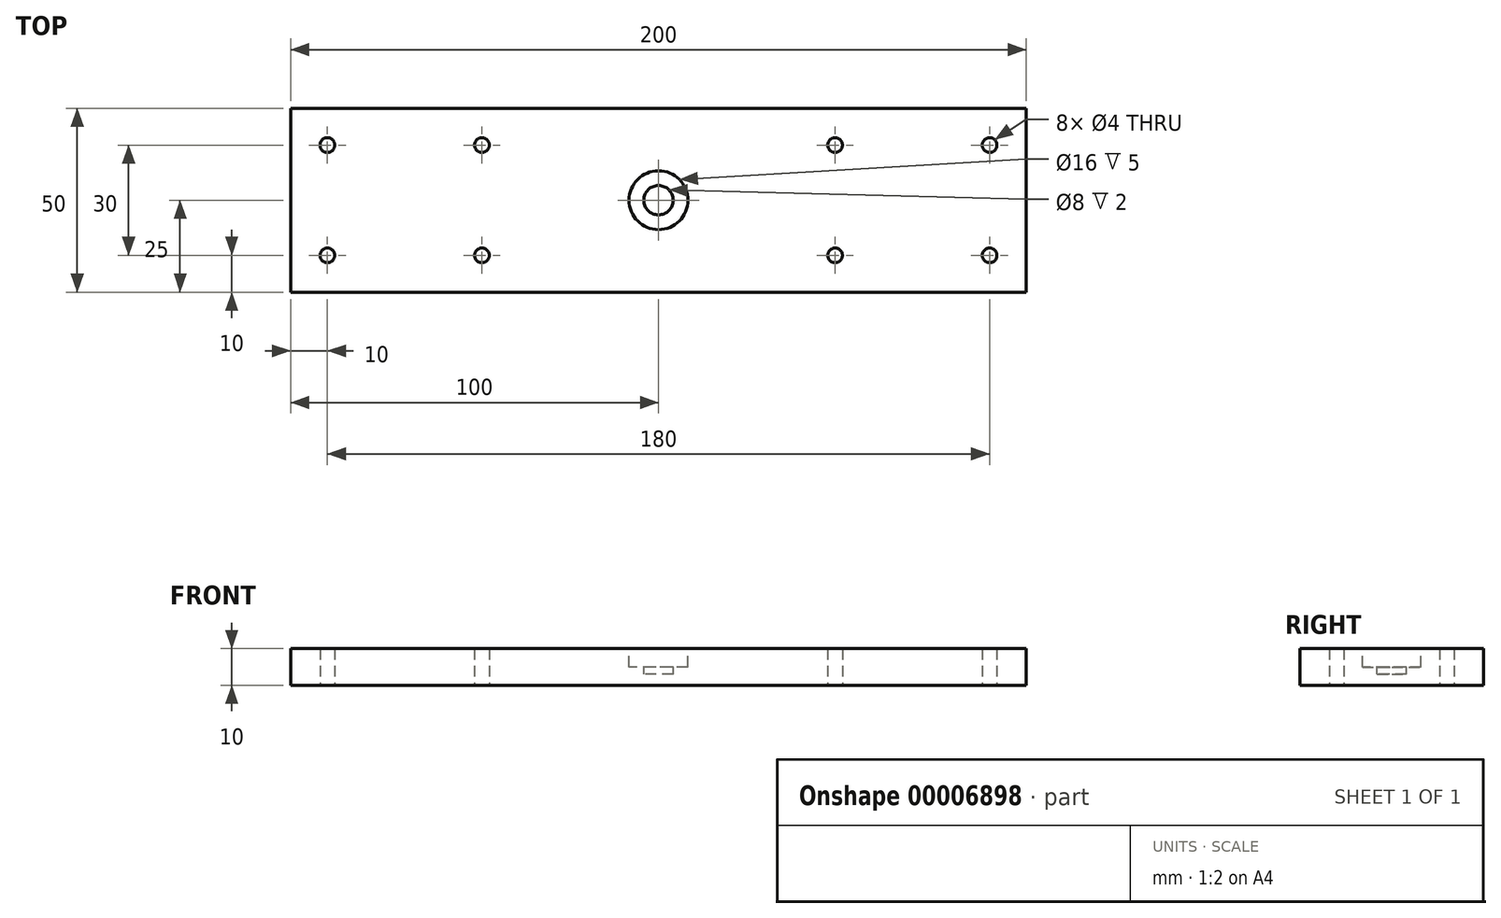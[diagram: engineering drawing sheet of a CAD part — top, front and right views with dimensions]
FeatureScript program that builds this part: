
annotation { "Feature Type Name" : "Feature", "Feature Type Description" : "" }
export const myFeature = defineFeature(function(context is Context, id is Id, definition is map)
    precondition{}
    {
        {
            var Q0;
            Q0=qCreatedBy(makeId("Top.planeOp"),FACE);
            var sketch = newSketch(context, id + "F0", { "sketchPlane" : qUnion([Q0])});
            skLineSegment(sketch, "E0.rect.bottom", {"start": v(100, -25) * mm, "end": v(-100, -25) * mm});
            skLineSegment(sketch, "E0.rect.top", {"start": v(100, 25) * mm, "end": v(-100, 25) * mm});
            skLineSegment(sketch, "E0.rect.left", {"start": v(100, -25) * mm, "end": v(100, 25) * mm});
            skLineSegment(sketch, "E0.rect.right", {"start": v(-100, -25) * mm, "end": v(-100, 25) * mm});
            skPoint(sketch, "E0.rect.middle", {"position": v(0, 0) * mm});
            skCircle(sketch, "E1", {"center": v(-90, 15) * mm, "radius": 2 * mm});
            skCircle(sketch, "E2", {"center": v(-48, 15) * mm, "radius": 2 * mm});
            skCircle(sketch, "E3", {"center": v(-90, -15) * mm, "radius": 2 * mm});
            skCircle(sketch, "E4", {"center": v(-48, -15) * mm, "radius": 2 * mm});
            skCircle(sketch, "E5", {"center": v(90, -15) * mm, "radius": 2 * mm});
            skCircle(sketch, "E6", {"center": v(48, -15) * mm, "radius": 2 * mm});
            skCircle(sketch, "E7", {"center": v(90, 15) * mm, "radius": 2 * mm});
            skCircle(sketch, "E8", {"center": v(48, 15) * mm, "radius": 2 * mm});
            skLineSegment(sketch, "E9", {"start": v(-113, 0) * mm, "end": v(185, 0) * mm, "construction": true});
            skLineSegment(sketch, "E10", {"start": v(0, 88.94) * mm, "end": v(0, -137.61) * mm, "construction": true});
            skSolve(sketch);
        }
        {
            var Q0;
            Q0=qSketchRegion(id+"F0",true);
            var Q1;
            Q1=makeQuery(id+"F0.imprint","IMPRINT",FACE,{"disambiguationData":[TD([[makeQuery(id+"F0.imprint","IMPRINT",EDGE,{"derivedFrom":sQuery(id+"F0.wireOp",EDGE,"E0.rect.bottom")}),-1.0]])]});
            extrude(context, id + "F1", {"entities" : qUnion([Q0, Q1]), "depth" : 10 * mm});
        }
        {
            var Q0;
            Q0=makeQuery(id+"F1.opExtrude","CAP_FACE",FACE,{"disambiguationData":[OSD([sQuery(id+"F0.wireOp",EDGE,"E0.rect.bottom"),sQuery(id+"F0.wireOp",EDGE,"E0.rect.top"),sQuery(id+"F0.wireOp",EDGE,"E0.rect.left"),sQuery(id+"F0.wireOp",EDGE,"E0.rect.right"),sQuery(id+"F0.wireOp",EDGE,"E1"),sQuery(id+"F0.wireOp",EDGE,"E2"),sQuery(id+"F0.wireOp",EDGE,"E3"),sQuery(id+"F0.wireOp",EDGE,"E4"),sQuery(id+"F0.wireOp",EDGE,"E5"),sQuery(id+"F0.wireOp",EDGE,"E6"),sQuery(id+"F0.wireOp",EDGE,"E7"),sQuery(id+"F0.wireOp",EDGE,"E8")])],"isStart":false});
            var sketch = newSketch(context, id + "F2", { "sketchPlane" : qUnion([Q0])});
            skCircle(sketch, "E11", {"center": v(0, 0) * mm, "radius": 8 * mm});
            skSolve(sketch);
        }
        {
            var Q0;
            Q0 = qSketchRegion(id + "F2", true);
            extrude(context, id + "F3", {"entities" : qUnion([Q0]), "operationType" : NewBodyOperationType.REMOVE, "oppositeDirection" : true, "depth" : (5) * mm});
        }
        {
            var Q0;
            Q0=makeQuery(id+"F3.boolean.opBoolean","COPY",FACE,{"derivedFrom":makeQuery(id+"F3.opExtrude","CAP_FACE",FACE,{"disambiguationData":[OSD([sQuery(id+"F2.wireOp",EDGE,"E11")])],"isStart":false})});
            var sketch = newSketch(context, id + "F4", { "sketchPlane" : qUnion([Q0])});
            skCircle(sketch, "E12", {"center": v(0, 0) * mm, "radius": 4 * mm});
            skSolve(sketch);
        }
        {
            var Q0;
            Q0 = qSketchRegion(id + "F4", true);
            extrude(context, id + "F5", {"entities" : qUnion([Q0]), "operationType" : NewBodyOperationType.REMOVE, "oppositeDirection" : true, "depth" : (2) * mm});
        }
    });
